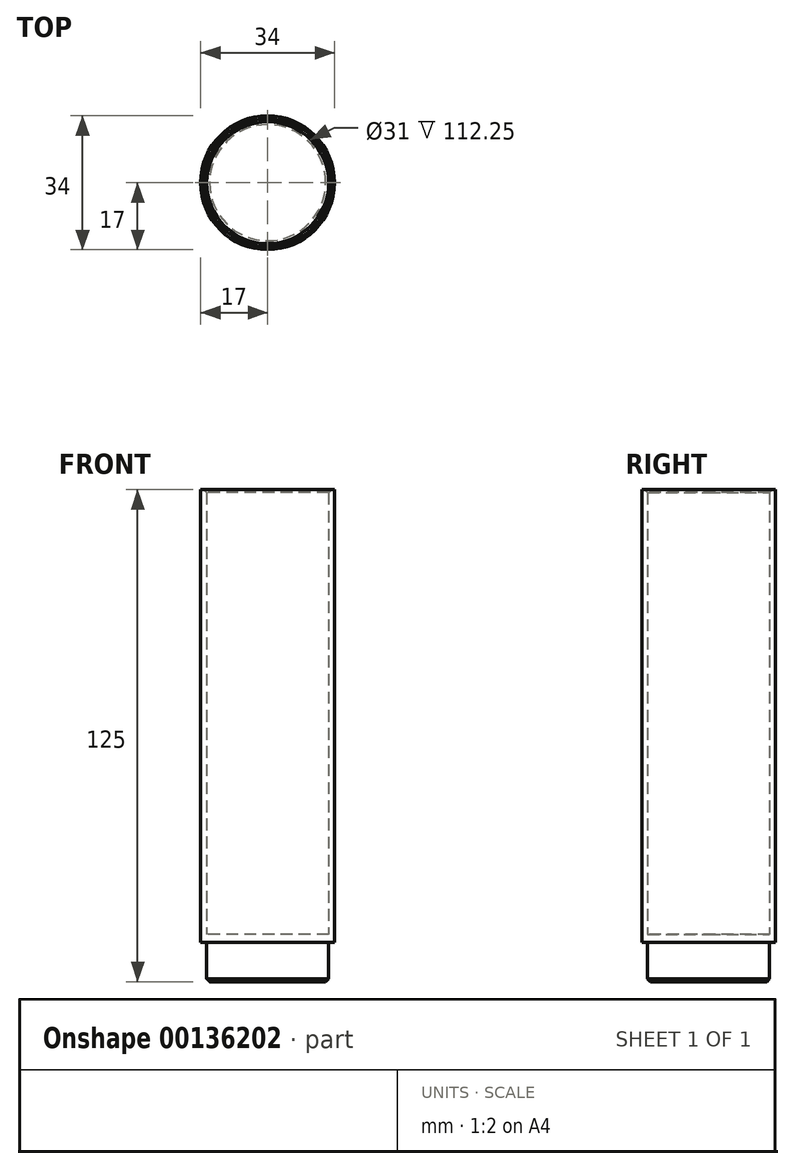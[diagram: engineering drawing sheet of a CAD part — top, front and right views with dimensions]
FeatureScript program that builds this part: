
annotation { "Feature Type Name" : "Feature", "Feature Type Description" : "" }
export const myFeature = defineFeature(function(context is Context, id is Id, definition is map)
    precondition{}
    {
        {
            var Q0;
            Q0=qCreatedBy(makeId("Top.planeOp"),FACE);
            cPlane(context, id + "F0", {"entities" : qUnion([Q0]), "cplaneType" : CPlaneType.OFFSET, "offset" : (222) * mm, "width" : 150 * mm, "height" : 150 * mm});
        }
        {
            var Q0;
            Q0=qCreatedBy(id+"F0.planeOp",FACE);
            var sketch = newSketch(context, id + "F1", { "sketchPlane" : qUnion([Q0])});
            skCircle(sketch, "E0", {"center": v(0, 0) * mm, "radius": 17 * mm});
            skCircle(sketch, "E1", {"center": v(0, 0) * mm, "radius": 15.5 * mm});
            skSolve(sketch);
        }
        {
            var Q0;
            Q0 = qSketchRegion(id + "F1", true);
            extrude(context, id + "F2", {"entities" : qUnion([Q0]), "depth" : 115 * mm});
        }
        {
            var Q0;
            Q0=makeQuery(id+"F2.opExtrude","CAP_EDGE",EDGE,{"disambiguationData":[OSD([sQuery(id+"F1.wireOp",EDGE,"E1")])],"isStart":false});
            chamfer(context, id + "F3", {"entities" : qUnion([Q0]), "width" : .75 * mm, "tangentPropagation" : true});
        }
        {
            var Q0;
            Q0=qCreatedBy(id+"F0.planeOp",FACE);
            var sketch = newSketch(context, id + "F4", { "sketchPlane" : qUnion([Q0])});
            skCircle(sketch, "E2.0", {"center": v(0, 0) * mm, "radius": 17 * mm});
            skSolve(sketch);
        }
        {
            var Q0;
            Q0=makeQuery(id+"F4.imprint","IMPRINT",FACE,{"disambiguationData":[TD([[makeQuery(id+"F4.imprint","IMPRINT",EDGE,{"derivedFrom":sQuery(id+"F4.wireOp",EDGE,"E2.0")}),1.0]])]});
            extrude(context, id + "F5", {"entities" : qUnion([Q0]), "operationType" : NewBodyOperationType.ADD, "depth" : 2 * mm});
        }
        {
            var Q0;
            Q0=makeQuery(id+"F5.boolean.opBoolean","MERGE",FACE,{"derivedFrom":[makeQuery(id+"F2.opExtrude","CAP_FACE",FACE,{"disambiguationData":[OSD([sQuery(id+"F1.wireOp",EDGE,"E0"),sQuery(id+"F1.wireOp",EDGE,"E1")])],"isStart":true}),makeQuery(id+"F5.opExtrude","CAP_FACE",FACE,{"disambiguationData":[OSD([sQuery(id+"F4.wireOp",EDGE,"E2.0")])],"isStart":true})]});
            var sketch = newSketch(context, id + "F6", { "sketchPlane" : qUnion([Q0])});
            skCircle(sketch, "E3", {"center": v(0, 0) * mm, "radius": 15.5 * mm});
            skSolve(sketch);
        }
        {
            var Q0;
            Q0 = qSketchRegion(id + "F6", true);
            extrude(context, id + "F7", {"entities" : qUnion([Q0]), "operationType" : NewBodyOperationType.ADD, "depth" : 10 * mm});
        }
        {
            var Q0;
            Q0=makeQuery(id+"F7.opExtrude","CAP_EDGE",EDGE,{"disambiguationData":[OSD([sQuery(id+"F6.wireOp",EDGE,"E3")])],"isStart":false});
            chamfer(context, id + "F8", {"entities" : qUnion([Q0]), "width" : .75 * mm, "tangentPropagation" : true});
        }
    });
